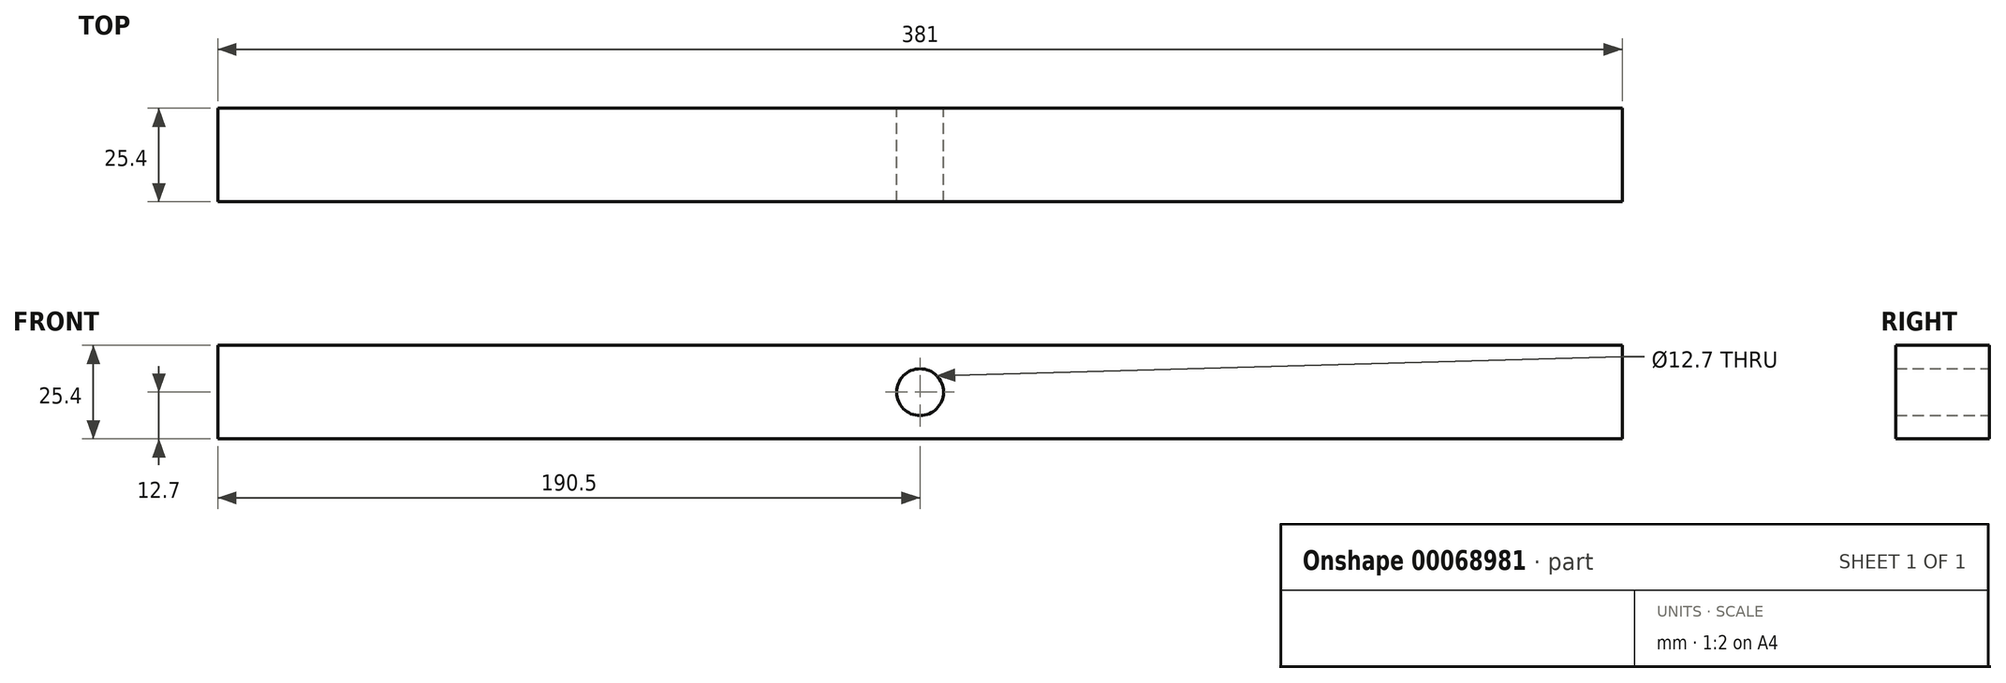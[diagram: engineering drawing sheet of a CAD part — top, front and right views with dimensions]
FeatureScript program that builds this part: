
annotation { "Feature Type Name" : "Feature", "Feature Type Description" : "" }
export const myFeature = defineFeature(function(context is Context, id is Id, definition is map)
    precondition{}
    {
        {
            var Q0;
            Q0=qCreatedBy(makeId("Front.planeOp"),FACE);
            var sketch = newSketch(context, id + "F0", { "sketchPlane" : qUnion([Q0])});
            skLineSegment(sketch, "E0.rect.bottom", {"start": v(190.5, 12.7) * mm, "end": v(-190.5, 12.7) * mm});
            skLineSegment(sketch, "E0.rect.top", {"start": v(190.5, -12.7) * mm, "end": v(-190.5, -12.7) * mm});
            skLineSegment(sketch, "E0.rect.left", {"start": v(190.5, 12.7) * mm, "end": v(190.5, -12.7) * mm});
            skLineSegment(sketch, "E0.rect.right", {"start": v(-190.5, 12.7) * mm, "end": v(-190.5, -12.7) * mm});
            skPoint(sketch, "E0.rect.middle", {"position": v(0, 0) * mm});
            skCircle(sketch, "E1", {"center": v(0, 0) * mm, "radius": 6.35 * mm});
            skSolve(sketch);
        }
        {
            var Q0;
            Q0 = qSketchRegion(id + "F0", true);
            extrude(context, id + "F1", {"entities" : qUnion([Q0]), "depth" : 25.4 * mm});
        }
    });
